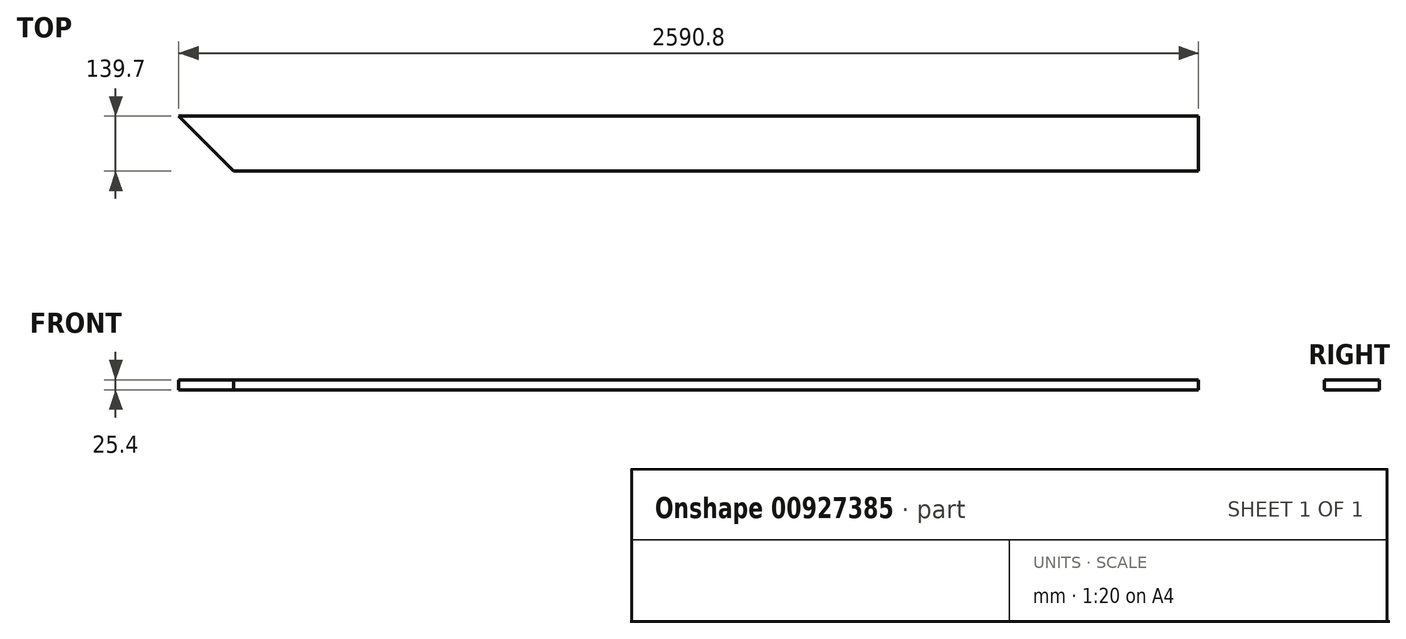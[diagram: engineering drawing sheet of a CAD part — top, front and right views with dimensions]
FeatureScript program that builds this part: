
annotation { "Feature Type Name" : "Feature", "Feature Type Description" : "" }
export const myFeature = defineFeature(function(context is Context, id is Id, definition is map)
    precondition{}
    {
        {
            var Q0;
            Q0=qCreatedBy(makeId("Top.planeOp"),FACE);
            var sketch = newSketch(context, id + "F0", { "sketchPlane" : qUnion([Q0])});
            skLineSegment(sketch, "E0", {"start": v(-2590.8, 69.85) * mm, "end": v(0, 69.85) * mm});
            skLineSegment(sketch, "E1", {"start": v(0, 69.85) * mm, "end": v(0, -69.85) * mm});
            skLineSegment(sketch, "E2", {"start": v(0, -69.85) * mm, "end": v(-2451.1, -69.85) * mm});
            skLineSegment(sketch, "E3", {"start": v(-2451.1, -69.85) * mm, "end": v(-2590.8, 69.85) * mm});
            skSolve(sketch);
        }
        {
            var Q0;
            Q0 = qSketchRegion(id + "F0", true);
            extrude(context, id + "F1", {"entities" : qUnion([Q0]), "depth" : 25.4 * mm, "offsetDistance" : 25.4 * mm});
        }
    });
